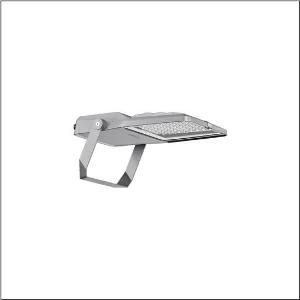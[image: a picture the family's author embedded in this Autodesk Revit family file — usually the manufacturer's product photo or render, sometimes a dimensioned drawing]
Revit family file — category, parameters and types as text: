
# Revit family: floodlight_fl_21_iq_mini___pl61_5xa7772b5c1a_2793
name_source: partatom
category: Lighting Fixtures
units: mm (PartAtom-declared; Revit-internal decimal feet)

## family parameters
Cut with Voids When Loaded = No
Host = Face
Light Source = No
Part Type = Normal
Room Calculation Point = No
Round Connector Dimension = Use Diameter
Shared = No

## types (1)
- --- (1 x LED, 5710 lm, 45.5 W, 4000K)
    Apparent Load = 46 VA
    CIE Flux Codes = 33 65 98 100 100
    Color Rendering = 80
    Color Temperature = 4000K
    Default Elevation = 1800 mm
    Description = Floodlight FL 21 iQ mini, floodlight, primary light control with lens, of PMMA, primary optical cover: protective disc, of toughened safety glass, transparent, light distribution: PL61, light emission: direct distribution, installation type: surface-mounted, lamps: LED, High Power LED, rated values: 5.710lm | 45,5W | 125,5lm/W (begin service life); end service life: 5.710lm | 48W; at 50% lumin. flux: 2.855lm | 21,5W | 132,8lm/W, colour temperature: 4000K, colour rendering: CRI > 80, light colour: 840, light setting 1 begin service life: 100% | 5.710lm | 45,5W | 125,5lm/W | 4.000K, light setting 1 end service life: 48W, further light settings possible, control: Street-Remote, Auto-Match, Temp-Guard, Night-Set, Smart-Wire, Desk-Remote (wireless, voltage-free reading and setting of iQ features in the workshop via application-optimized NFC function/RFID function), optimised constant luminous flux control (CLO 2.0), pre-setting: linear dimming characteristic, with terminal, 6-pole, mains connection: 220..240V, AC, 50/60Hz, luminaire housing, of diecast aluminium, powder-coated, SITECO metallic grey (DB 702S), corrosivity category C5 mid according to DIN EN ISO 12944suitable for swimming poolschlorine-resistant, sealing non-destructively replaceable, mounting bracket, of steel, galvanised, powder-coated, SITECO metallic grey (DB 702S), protection rating (complete): IP66, insulation class (complete): insulation class II (safety insulation), certification: CE, ENEC, VDE, protection symbol: D, impact resistance: IK08, permissible operating ambient temperature: -40..+40°C, permissible operating ambient temperature for outdoor applications: -40..+50°C, standard: DIN EN 12944, LABS conformity tested according to VDMA 24364:2018-05, packaging unit: 1 piece

Light Distribution: PL61
    Height = 70 mm
    Lamp = 1 x LED
    Lamp Light Flux = 5710 lm
    Lamp Power = 45.5 W
    Lamp count = 1
    Length = 485 mm
    Luminous efficacy = 125 lm/W
    Manufacturer = Siteco
    ModVariant = No
    Model = 5XA7772B5C1A
    Mounting Place = Pole
    Mounting Type = Pole annexe
    Number of Poles = 1
    OnlyDefault = Yes
    Power Factor = 1
    Product Name = Floodlight FL 21 iQ mini | PL61
    Product group = floodlight | pylon annexe
    ProductGroupID = 6201
    Protection Class = Protection class II
    Protection Degree = IP 66
    RLX_Detail_Level = 1
    RLX_Emergency_Light_Flux = 0 lm
    RLX_Emergency_Type = 0
    RLX_Emergency_Type_DB = No
    RlxData = <blob elided: 96405 chars, md5=cfe3a3fe>
    Socket = socket
    Standby Power = 0 W
    System Light Flux = 5710 lm
    System Power = 46 W
    Type Comments = factory setting: luminous flux: 100 % | dim-lin: 254 | 463 mA
    Type Image = l_1006845.jpg
    URL = http://relux.com
    VarID = @adj_174445
    Voltage = 0 V
    Weight = 0.00 kg
    Width = 337 mm

## geometry (parser evidence)
native form markers: Blend x4, Sweep x12
no freeform markers — native parametric forms only
